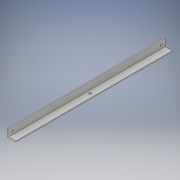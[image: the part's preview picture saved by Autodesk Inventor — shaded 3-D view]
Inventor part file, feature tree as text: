
AUTODESK INVENTOR PART (.ipt)
format: ipt  version: 2017 (Build 210142000, 142)  size: 120,320 bytes
history: native  units: in
note: dims shown in document units (in); Inventor stores cm internally (conversion verified against a paired STEP export)
features: hole x2, sketch x2, extrude x1
ambient origin geometry x8: Origin, YZ Plane, XZ Plane, XY Plane, X Axis, Y Axis, Z Axis, Center Point
bodies: Solid1 (feature_tree)
feature tree (5):
  extrude  "Extrusion1"  Depth=1.0in
  hole  "mount"  [1 undecoded]
  hole  "Hole5"  [1 undecoded]
  sketch  "Sketch7"  dims[d0=1.0in d1=1.0in]
  sketch  "Sketch8"  dims[d2=0.125in d3=19.375in d4=0.0in d43=0.5in d44=0.5in d45=0.7874in d47=18.375in d48=0.3937in d50=1.0in d52=0.266in d53=0.75in d54=0.507in d55=0.25in d56=0.5635in d57=1.0in d58=0.8108in d59=0.5in d60=0.266in d61=0.75in d62=0.507in d63=0.25in d64=0.5635in d65=1.0in d66=0.8108in]
note: 2 required parameter values undecoded (feature->parameter linkage not recoverable at this tier; creation-order binding heuristic only, values carry confidence <= 0.55)
